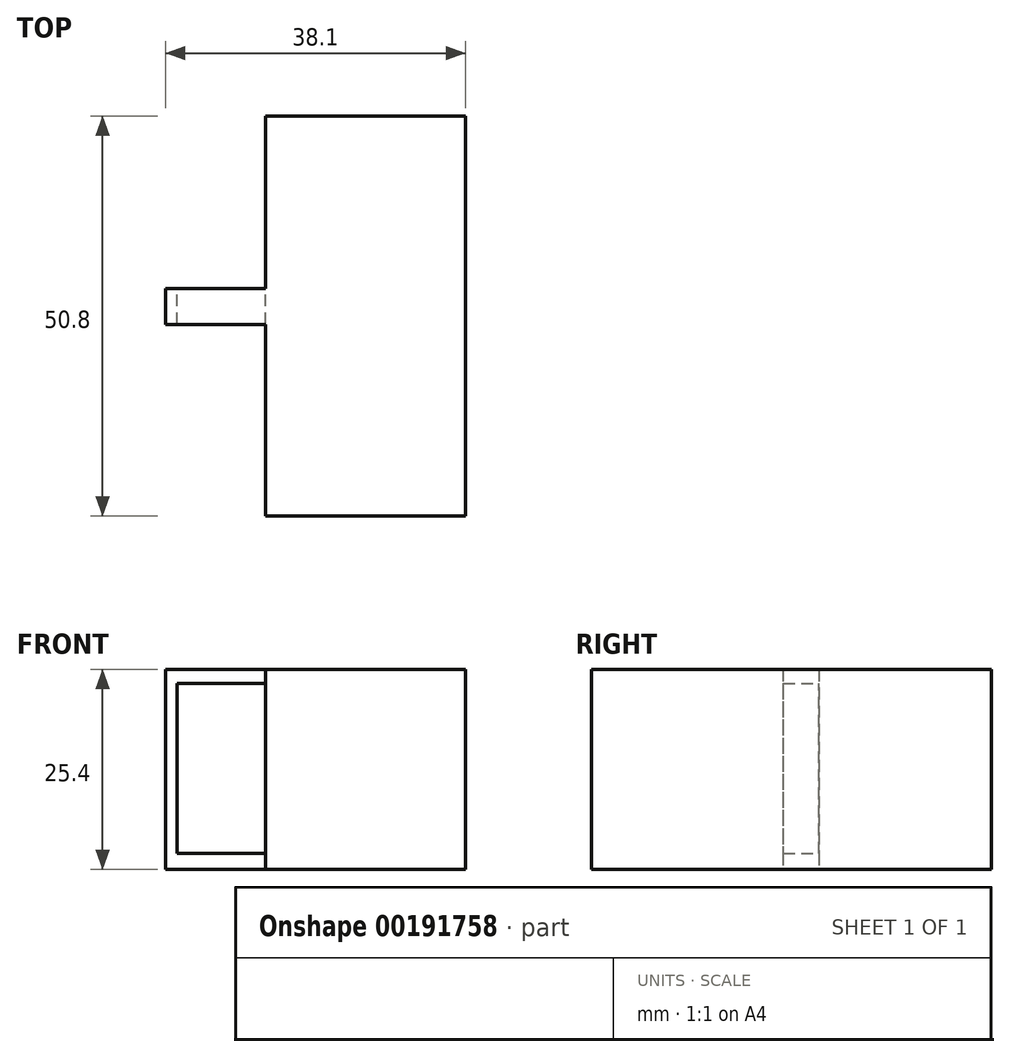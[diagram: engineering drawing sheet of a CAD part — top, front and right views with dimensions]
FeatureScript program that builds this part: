
annotation { "Feature Type Name" : "Feature", "Feature Type Description" : "" }
export const myFeature = defineFeature(function(context is Context, id is Id, definition is map)
    precondition{}
    {
        {
            var Q0;
            Q0=qCreatedBy(makeId("Front.planeOp"),FACE);
            var sketch = newSketch(context, id + "F0", { "sketchPlane" : qUnion([Q0])});
            skLineSegment(sketch, "E0.bottom", {"start": v(-34.15, 25.4) * mm, "end": v(-8.75, 25.4) * mm});
            skLineSegment(sketch, "E0.top", {"start": v(-34.15, 0) * mm, "end": v(-8.75, 0) * mm});
            skLineSegment(sketch, "E0.left", {"start": v(-34.15, 25.4) * mm, "end": v(-34.15, 0) * mm});
            skLineSegment(sketch, "E0.right", {"start": v(-8.75, 25.4) * mm, "end": v(-8.75, 0) * mm});
            skSolve(sketch);
        }
        {
            var Q0;
            Q0 = qSketchRegion(id + "F0", true);
            extrude(context, id + "F1", {"entities" : qUnion([Q0]), "depth" : 50.8 * mm});
        }
        {
            var Q0;
            Q0=makeQuery(id+"F1.opExtrude","SWEPT_FACE",FACE,{"disambiguationData":[OSD([sQuery(id+"F0.wireOp",EDGE,"E0.left")])]});
            var sketch = newSketch(context, id + "F2", { "sketchPlane" : qUnion([Q0])});
            skLineSegment(sketch, "E1.bottom", {"start": v(21.9, 25.4) * mm, "end": v(26.46, 25.4) * mm});
            skLineSegment(sketch, "E1.top", {"start": v(21.9, 0) * mm, "end": v(26.46, 0) * mm});
            skLineSegment(sketch, "E1.left", {"start": v(21.9, 25.4) * mm, "end": v(21.9, 0) * mm});
            skLineSegment(sketch, "E1.right", {"start": v(26.46, 25.4) * mm, "end": v(26.46, 0) * mm});
            skSolve(sketch);
        }
        {
            var Q0;
            Q0 = qSketchRegion(id + "F2", true);
            extrude(context, id + "F3", {"entities" : qUnion([Q0]), "operationType" : NewBodyOperationType.ADD, "depth" : 12.7 * mm});
        }
        {
            var Q0;
            Q0=makeQuery(id+"F3.opExtrude","SWEPT_FACE",FACE,{"disambiguationData":[OSD([sQuery(id+"F2.wireOp",EDGE,"E1.left")])]});
            var sketch = newSketch(context, id + "F4", { "sketchPlane" : qUnion([Q0])});
            skLineSegment(sketch, "E2.bottom", {"start": v(34.15, 2.02) * mm, "end": v(45.4, 2.02) * mm});
            skLineSegment(sketch, "E2.top", {"start": v(34.15, 23.63) * mm, "end": v(45.4, 23.63) * mm});
            skLineSegment(sketch, "E2.left", {"start": v(34.15, 2.02) * mm, "end": v(34.15, 23.63) * mm});
            skLineSegment(sketch, "E2.right", {"start": v(45.4, 2.02) * mm, "end": v(45.4, 23.63) * mm});
            skSolve(sketch);
        }
        {
            var Q0;
            Q0=makeQuery(id+"F4.imprint","IMPRINT",FACE,{"disambiguationData":[TD([[makeQuery(id+"F4.imprint","IMPRINT",EDGE,{"derivedFrom":sQuery(id+"F4.wireOp",EDGE,"E2.bottom")}),1.0]])]});
            extrude(context, id + "F5", {"entities" : qUnion([Q0]), "operationType" : NewBodyOperationType.REMOVE, "oppositeDirection" : true, "depth" : 25.4 * mm});
        }
    });
